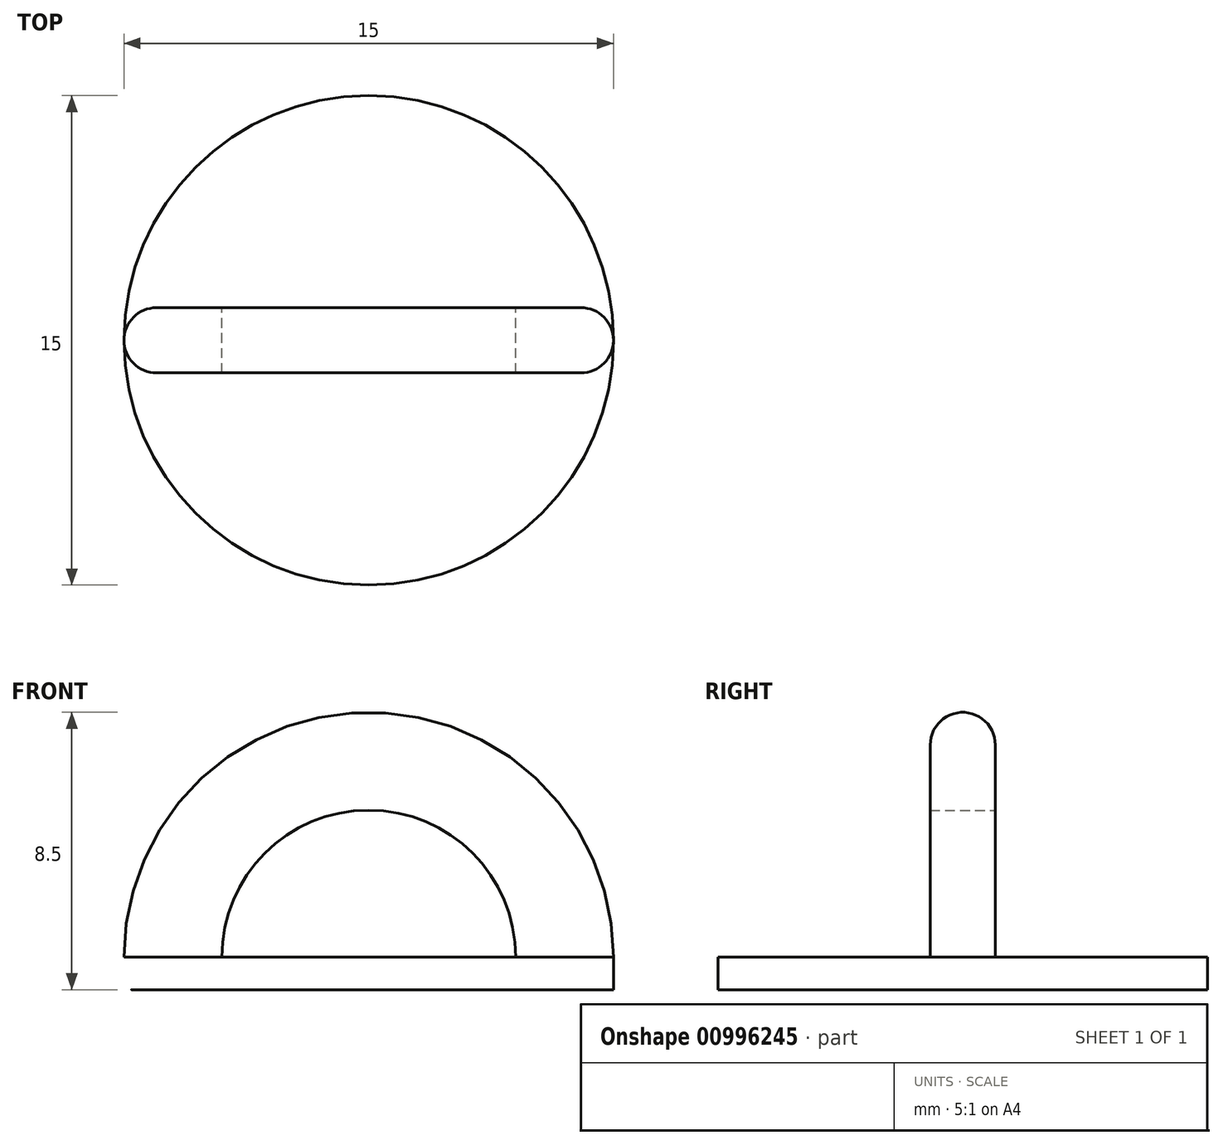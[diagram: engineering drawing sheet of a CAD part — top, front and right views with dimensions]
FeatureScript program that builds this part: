
annotation { "Feature Type Name" : "Feature", "Feature Type Description" : "" }
export const myFeature = defineFeature(function(context is Context, id is Id, definition is map)
    precondition{}
    {
        {
            var Q0;
            Q0=qCreatedBy(makeId("Top.planeOp"),FACE);
            var sketch = newSketch(context, id + "F0", { "sketchPlane" : qUnion([Q0])});
            skCircle(sketch, "E0", {"center": v(0, 0) * mm, "radius": 7.5 * mm});
            skSolve(sketch);
        }
        {
            var Q0;
            Q0 = qSketchRegion(id + "F0", true);
            extrude(context, id + "F1", {"entities" : qUnion([Q0]), "depth" : 1 * mm, "offsetDistance" : 25 * mm});
        }
        {
            var Q0;
            Q0=qCreatedBy(makeId("Front.planeOp"),FACE);
            var sketch = newSketch(context, id + "F2", { "sketchPlane" : qUnion([Q0])});
            skLineSegment(sketch, "E1.0", {"start": v(-7.5, 1) * mm, "end": v(7.5, 1) * mm, "construction": true});
            skArc(sketch, "E2", {"start": v(-4.5, 1) * mm, "mid": v(0, 5.5) * mm, "end": v(4.5, 1) * mm});
            skArc(sketch, "E3.0", {"start": v(-7.5, 1) * mm, "mid": v(0, 8.5) * mm, "end": v(7.5, 1) * mm});
            skLineSegment(sketch, "E4", {"start": v(0, 1) * mm, "end": v(0, 11.48) * mm, "construction": true});
            skLineSegment(sketch, "E5", {"start": v(-4.5, 1) * mm, "end": v(-7.5, 1) * mm});
            skLineSegment(sketch, "E6", {"start": v(7.5, 1) * mm, "end": v(4.5, 1) * mm});
            skSolve(sketch);
        }
        {
            var Q0;
            Q0 = qSketchRegion(id + "F2", true);
            extrude(context, id + "F3", {"entities" : qUnion([Q0]), "operationType" : NewBodyOperationType.ADD, "endBound" : BoundingType.SYMMETRIC, "depth" : 2 * mm, "offsetDistance" : 25 * mm});
        }
        {
            var Q0;
            Q0=makeQuery(id+"F1.opExtrude","CAP_FACE",FACE,{"disambiguationData":[OSD([sQuery(id+"F0.wireOp",EDGE,"E0")])],"isStart":true});
            var sketch = newSketch(context, id + "F4", { "sketchPlane" : qUnion([Q0])});
            skCircle(sketch, "E7.0", {"center": v(0, 0) * mm, "radius": 11 * mm});
            skSolve(sketch);
        }
        {
            var Q0;
            Q0=makeQuery(id+"F4.imprint","IMPRINT",FACE,{"disambiguationData":[TD([[makeQuery(id+"F4.imprint","IMPRINT",EDGE,{"derivedFrom":sQuery(id+"F4.wireOp",EDGE,"E7.0")}),1.0]])]});
            extrude(context, id + "F5", {"entities" : qUnion([Q0]), "operationType" : NewBodyOperationType.REMOVE, "endBound" : BoundingType.THROUGH_ALL, "oppositeDirection" : true, "depth" : 25 * mm, "offsetDistance" : 25 * mm});
        }
        {
            var Q0;
            Q0=makeQuery(id+"F3.opExtrude","CAP_EDGE",EDGE,{"disambiguationData":[OSD([sQuery(id+"F2.wireOp",EDGE,"E3.0")])],"isStart":false});
            var Q1;
            Q1=makeQuery(id+"F3.opExtrude","CAP_EDGE",EDGE,{"disambiguationData":[OSD([sQuery(id+"F2.wireOp",EDGE,"E3.0")])],"isStart":true});
            fillet(context, id + "F6", {"entities" : qUnion([Q0, Q1]), "radius" : 1 * mm, "tangentPropagation" : true, "allowEdgeOverflow" : false});
        }
    });
